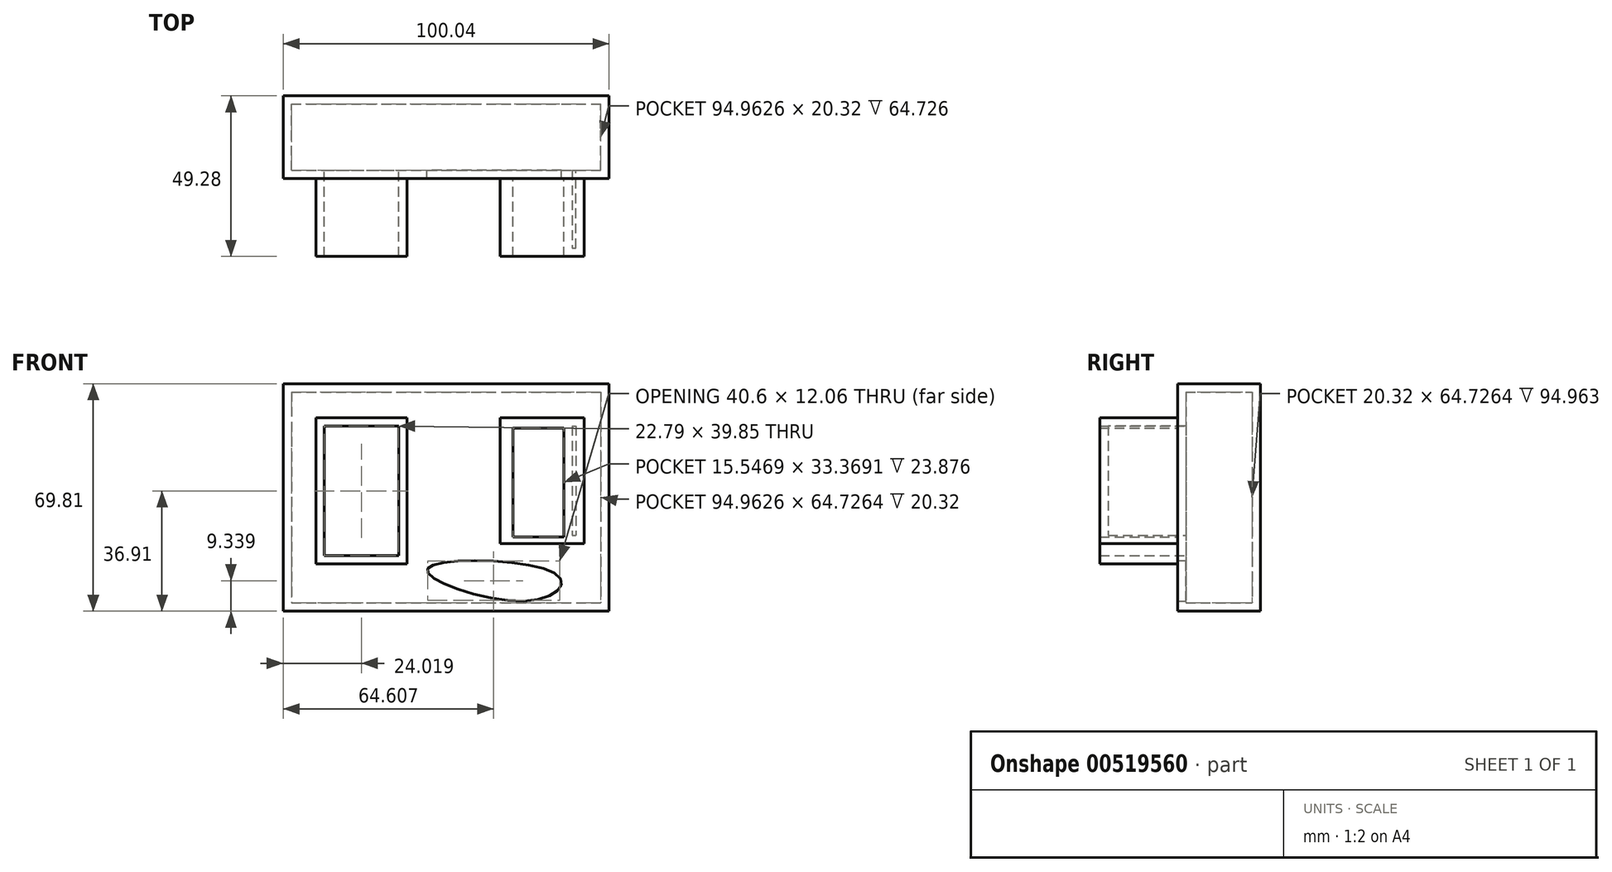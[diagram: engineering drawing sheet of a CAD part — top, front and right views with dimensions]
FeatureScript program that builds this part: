
annotation { "Feature Type Name" : "Feature", "Feature Type Description" : "" }
export const myFeature = defineFeature(function(context is Context, id is Id, definition is map)
    precondition{}
    {
        {
            var Q0;
            Q0=qCreatedBy(makeId("Front.planeOp"),FACE);
            var sketch = newSketch(context, id + "F0", { "sketchPlane" : qUnion([Q0])});
            skLineSegment(sketch, "E0.bottom", {"start": v(-54.26, 49.1) * mm, "end": v(45.78, 49.1) * mm});
            skLineSegment(sketch, "E0.top", {"start": v(-54.26, -20.7) * mm, "end": v(45.78, -20.7) * mm});
            skLineSegment(sketch, "E0.left", {"start": v(-54.26, 49.1) * mm, "end": v(-54.26, -20.7) * mm});
            skLineSegment(sketch, "E0.right", {"start": v(45.78, 49.1) * mm, "end": v(45.78, -20.7) * mm});
            skSolve(sketch);
        }
        {
            var Q0;
            Q0 = qSketchRegion(id + "F0", true);
            extrude(context, id + "F1", {"entities" : qUnion([Q0]), "depth" : 25.4 * mm, "offsetDistance" : 25.4 * mm});
        }
        {
            var Q0;
            Q0=makeQuery(id+"F1.opExtrude","CAP_FACE",FACE,{"disambiguationData":[OSD([sQuery(id+"F0.wireOp",EDGE,"E0.bottom"),sQuery(id+"F0.wireOp",EDGE,"E0.top"),sQuery(id+"F0.wireOp",EDGE,"E0.left"),sQuery(id+"F0.wireOp",EDGE,"E0.right")])],"isStart":false});
            var sketch = newSketch(context, id + "F2", { "sketchPlane" : qUnion([Q0])});
            skLineSegment(sketch, "E1.bottom", {"start": v(-44.18, 38.68) * mm, "end": v(-16.3, 38.68) * mm});
            skLineSegment(sketch, "E1.top", {"start": v(-44.18, 22) * mm, "end": v(-16.3, 22) * mm});
            skLineSegment(sketch, "E1.left", {"start": v(-44.18, 38.68) * mm, "end": v(-44.18, 22) * mm});
            skLineSegment(sketch, "E1.right", {"start": v(-16.3, 38.68) * mm, "end": v(-16.3, 22) * mm});
            skLineSegment(sketch, "E2.bottom", {"start": v(12.32, 38.68) * mm, "end": v(38.1, 38.68) * mm});
            skLineSegment(sketch, "E2.top", {"start": v(12.32, 0) * mm, "end": v(38.1, 0) * mm});
            skLineSegment(sketch, "E2.left", {"start": v(12.32, 38.68) * mm, "end": v(12.32, 0) * mm});
            skLineSegment(sketch, "E2.right", {"start": v(38.1, 38.68) * mm, "end": v(38.1, 0) * mm});
            skPoint(sketch, "E3.oppositeSnap0", {"position": v(-30.24, 22) * mm});
            skLineSegment(sketch, "E3.bottom", {"start": v(-30.24, 22) * mm, "end": v(-30.24, 22) * mm});
            skLineSegment(sketch, "E3.top", {"start": v(-30.24, 0) * mm, "end": v(-30.24, 0) * mm});
            skLineSegment(sketch, "E3.left", {"start": v(-30.24, 22) * mm, "end": v(-30.24, 0) * mm});
            skLineSegment(sketch, "E3.right", {"start": v(-30.24, 22) * mm, "end": v(-30.24, 0) * mm});
            skLineSegment(sketch, "E4.bottom", {"start": v(-16.3, 22) * mm, "end": v(-16.3, 22) * mm});
            skLineSegment(sketch, "E4.top", {"start": v(-16.3, 0) * mm, "end": v(-16.3, 0) * mm});
            skLineSegment(sketch, "E4.left", {"start": v(-16.3, 22) * mm, "end": v(-16.3, 0) * mm});
            skLineSegment(sketch, "E4.right", {"start": v(-16.3, 22) * mm, "end": v(-16.3, 0) * mm});
            skLineSegment(sketch, "E5.top", {"start": v(-44.18, -6.26) * mm, "end": v(-16.3, -6.26) * mm});
            skLineSegment(sketch, "E5.left", {"start": v(-44.18, 22) * mm, "end": v(-44.18, -6.26) * mm});
            skLineSegment(sketch, "E5.right", {"start": v(-16.3, 22) * mm, "end": v(-16.3, -6.26) * mm});
            skLineSegment(sketch, "E6.bottom", {"start": v(-16.3, -6.26) * mm, "end": v(-44.18, -6.26) * mm});
            skLineSegment(sketch, "E6.top", {"start": v(-16.3, 22) * mm, "end": v(-44.18, 22) * mm});
            skLineSegment(sketch, "E6.left", {"start": v(-16.3, -6.26) * mm, "end": v(-16.3, 22) * mm});
            skLineSegment(sketch, "E6.right", {"start": v(-44.18, -6.26) * mm, "end": v(-44.18, 22) * mm});
            skLineSegment(sketch, "E7.bottom", {"start": v(-44.18, 22) * mm, "end": v(-44.18, 22) * mm});
            skLineSegment(sketch, "E7.top", {"start": v(-44.18, 0) * mm, "end": v(-44.18, 0) * mm});
            skLineSegment(sketch, "E7.left", {"start": v(-44.18, 22) * mm, "end": v(-44.18, 0) * mm});
            skLineSegment(sketch, "E7.right", {"start": v(-44.18, 22) * mm, "end": v(-44.18, 0) * mm});
            skLineSegment(sketch, "E8.bottom", {"start": v(-16.3, -2.09) * mm, "end": v(-44.18, -2.09) * mm});
            skLineSegment(sketch, "E8.left", {"start": v(-16.3, -2.09) * mm, "end": v(-16.3, -6.26) * mm});
            skLineSegment(sketch, "E8.right", {"start": v(-44.18, -2.09) * mm, "end": v(-44.18, -6.26) * mm});
            skLineSegment(sketch, "E9.bottom", {"start": v(-44.18, -2.09) * mm, "end": v(-16.3, -2.09) * mm});
            skLineSegment(sketch, "E9.top", {"start": v(-44.18, -2.09) * mm, "end": v(-16.3, -2.09) * mm});
            skLineSegment(sketch, "E9.left", {"start": v(-44.18, -2.09) * mm, "end": v(-44.18, -2.09) * mm});
            skLineSegment(sketch, "E9.right", {"start": v(-16.3, -2.09) * mm, "end": v(-16.3, -2.09) * mm});
            skLineSegment(sketch, "E10.bottom", {"start": v(-16.3, 0) * mm, "end": v(-44.18, 0) * mm});
            skLineSegment(sketch, "E10.top", {"start": v(-16.3, 0) * mm, "end": v(-44.18, 0) * mm});
            skLineSegment(sketch, "E11.top", {"start": v(-44.18, 0) * mm, "end": v(-16.3, 0) * mm});
            skLineSegment(sketch, "E12.bottom", {"start": v(-22, 38.68) * mm, "end": v(-22.18, 38.68) * mm});
            skLineSegment(sketch, "E12.top", {"start": v(-22, 22) * mm, "end": v(-22.18, 22) * mm});
            skLineSegment(sketch, "E12.left", {"start": v(-22, 38.68) * mm, "end": v(-22, 22) * mm});
            skLineSegment(sketch, "E12.right", {"start": v(-22.18, 38.68) * mm, "end": v(-22.18, 22) * mm});
            skLineSegment(sketch, "E13.bottom", {"start": v(-37.92, 38.68) * mm, "end": v(-37.73, 38.68) * mm});
            skLineSegment(sketch, "E13.top", {"start": v(-37.92, 22) * mm, "end": v(-37.73, 22) * mm});
            skLineSegment(sketch, "E13.left", {"start": v(-37.92, 38.68) * mm, "end": v(-37.92, 22) * mm});
            skLineSegment(sketch, "E13.right", {"start": v(-37.73, 38.68) * mm, "end": v(-37.73, 22) * mm});
            skLineSegment(sketch, "E14.bottom", {"start": v(-44.18, 7.87) * mm, "end": v(-16.3, 7.87) * mm});
            skLineSegment(sketch, "E14.top", {"start": v(-44.18, 7.87) * mm, "end": v(-16.3, 7.87) * mm});
            skLineSegment(sketch, "E14.left", {"start": v(-44.18, 7.87) * mm, "end": v(-44.18, 7.87) * mm});
            skLineSegment(sketch, "E14.right", {"start": v(-16.3, 7.87) * mm, "end": v(-16.3, 7.87) * mm});
            skLineSegment(sketch, "E15.bottom", {"start": v(-16.3, 12.9) * mm, "end": v(-44.18, 12.9) * mm});
            skLineSegment(sketch, "E15.top", {"start": v(-16.3, 11) * mm, "end": v(-44.18, 11) * mm});
            skLineSegment(sketch, "E15.left", {"start": v(-16.3, 12.9) * mm, "end": v(-16.3, 11) * mm});
            skLineSegment(sketch, "E15.right", {"start": v(-44.18, 12.9) * mm, "end": v(-44.18, 11) * mm});
            skLineSegment(sketch, "E16.bottom", {"start": v(-44.18, 16.87) * mm, "end": v(-16.3, 16.87) * mm});
            skLineSegment(sketch, "E16.top", {"start": v(-44.18, 19.72) * mm, "end": v(-16.3, 19.72) * mm});
            skLineSegment(sketch, "E16.left", {"start": v(-44.18, 16.87) * mm, "end": v(-44.18, 19.72) * mm});
            skLineSegment(sketch, "E16.right", {"start": v(-16.3, 16.87) * mm, "end": v(-16.3, 19.72) * mm});
            skLineSegment(sketch, "E17.bottom", {"start": v(12.32, 6.45) * mm, "end": v(38.1, 6.45) * mm});
            skLineSegment(sketch, "E17.top", {"start": v(12.32, 7.77) * mm, "end": v(38.1, 7.77) * mm});
            skLineSegment(sketch, "E17.left", {"start": v(12.32, 6.45) * mm, "end": v(12.32, 7.77) * mm});
            skLineSegment(sketch, "E17.right", {"start": v(38.1, 6.45) * mm, "end": v(38.1, 7.77) * mm});
            skLineSegment(sketch, "E18.bottom", {"start": v(38.1, 11.38) * mm, "end": v(12.32, 11.38) * mm});
            skLineSegment(sketch, "E18.top", {"start": v(38.1, 12.9) * mm, "end": v(12.32, 12.9) * mm});
            skLineSegment(sketch, "E18.left", {"start": v(38.1, 11.38) * mm, "end": v(38.1, 12.9) * mm});
            skLineSegment(sketch, "E18.right", {"start": v(12.32, 11.38) * mm, "end": v(12.32, 12.9) * mm});
            skLineSegment(sketch, "E19.bottom", {"start": v(12.32, 17.44) * mm, "end": v(38.1, 17.44) * mm});
            skLineSegment(sketch, "E19.top", {"start": v(12.32, 15.36) * mm, "end": v(38.1, 15.36) * mm});
            skLineSegment(sketch, "E19.left", {"start": v(12.32, 17.44) * mm, "end": v(12.32, 15.36) * mm});
            skLineSegment(sketch, "E19.right", {"start": v(38.1, 17.44) * mm, "end": v(38.1, 15.36) * mm});
            skPoint(sketch, "E20.oppositeSnap0", {"position": v(12.32, 19.34) * mm});
            skLineSegment(sketch, "E20.bottom", {"start": v(38.1, 19.34) * mm, "end": v(12.32, 19.34) * mm});
            skLineSegment(sketch, "E20.top", {"start": v(38.1, 22) * mm, "end": v(12.32, 22) * mm});
            skLineSegment(sketch, "E20.left", {"start": v(38.1, 19.34) * mm, "end": v(38.1, 22) * mm});
            skLineSegment(sketch, "E20.right", {"start": v(12.32, 19.34) * mm, "end": v(12.32, 22) * mm});
            skLineSegment(sketch, "E21.bottom", {"start": v(12.32, 24.65) * mm, "end": v(38.1, 24.65) * mm});
            skLineSegment(sketch, "E21.top", {"start": v(12.32, 30.15) * mm, "end": v(38.1, 30.15) * mm});
            skLineSegment(sketch, "E21.left", {"start": v(12.32, 24.65) * mm, "end": v(12.32, 30.15) * mm});
            skLineSegment(sketch, "E21.right", {"start": v(38.1, 24.65) * mm, "end": v(38.1, 30.15) * mm});
            skLineSegment(sketch, "E22.bottom", {"start": v(16.3, 38.68) * mm, "end": v(21.42, 38.68) * mm});
            skLineSegment(sketch, "E22.top", {"start": v(16.3, 0) * mm, "end": v(21.42, 0) * mm});
            skLineSegment(sketch, "E22.left", {"start": v(16.3, 38.68) * mm, "end": v(16.3, 0) * mm});
            skLineSegment(sketch, "E22.right", {"start": v(21.42, 38.68) * mm, "end": v(21.42, 0) * mm});
            skLineSegment(sketch, "E23.bottom", {"start": v(26.73, 38.68) * mm, "end": v(31.85, 38.68) * mm});
            skLineSegment(sketch, "E23.top", {"start": v(26.73, 0) * mm, "end": v(31.85, 0) * mm});
            skLineSegment(sketch, "E23.left", {"start": v(26.73, 38.68) * mm, "end": v(26.73, 0) * mm});
            skLineSegment(sketch, "E23.right", {"start": v(31.85, 38.68) * mm, "end": v(31.85, 0) * mm});
            skLineSegment(sketch, "E24.bottom", {"start": v(12.32, 33.56) * mm, "end": v(38.1, 33.56) * mm});
            skLineSegment(sketch, "E24.top", {"start": v(12.32, 35.45) * mm, "end": v(38.1, 35.45) * mm});
            skLineSegment(sketch, "E24.left", {"start": v(12.32, 33.56) * mm, "end": v(12.32, 35.45) * mm});
            skLineSegment(sketch, "E24.right", {"start": v(38.1, 33.56) * mm, "end": v(38.1, 35.45) * mm});
            skLineSegment(sketch, "E25.bottom", {"start": v(12.32, 3.6) * mm, "end": v(38.1, 3.6) * mm});
            skLineSegment(sketch, "E25.top", {"start": v(12.32, 2.09) * mm, "end": v(38.1, 2.09) * mm});
            skLineSegment(sketch, "E25.left", {"start": v(12.32, 3.6) * mm, "end": v(12.32, 2.09) * mm});
            skLineSegment(sketch, "E25.right", {"start": v(38.1, 3.6) * mm, "end": v(38.1, 2.09) * mm});
            skSolve(sketch);
        }
        {
            var Q0;
            Q0 = qSketchRegion(id + "F2", true);
            extrude(context, id + "F3", {"entities" : qUnion([Q0]), "operationType" : NewBodyOperationType.ADD, "depth" : 23.88 * mm, "offsetDistance" : 25.4 * mm});
        }
        {
            var Q0;
            Q0=makeQuery(id+"F3.opExtrude","CAP_FACE",FACE,{"disambiguationData":[OSD([sQuery(id+"F2.wireOp",EDGE,"E1.bottom"),sQuery(id+"F2.wireOp",EDGE,"E1.left"),sQuery(id+"F2.wireOp",EDGE,"E1.right"),sQuery(id+"F2.wireOp",EDGE,"E6.left"),sQuery(id+"F2.wireOp",EDGE,"E6.right"),sQuery(id+"F2.wireOp",EDGE,"E6.bottom"),sQuery(id+"F2.wireOp",EDGE,"E8.left"),sQuery(id+"F2.wireOp",EDGE,"E8.right"),sQuery(id+"F2.wireOp",EDGE,"E7.left"),sQuery(id+"F2.wireOp",EDGE,"E4.left"),sQuery(id+"F2.wireOp",EDGE,"E12.bottom"),sQuery(id+"F2.wireOp",EDGE,"E13.bottom"),sQuery(id+"F2.wireOp",EDGE,"E15.left"),sQuery(id+"F2.wireOp",EDGE,"E15.right"),sQuery(id+"F2.wireOp",EDGE,"E16.left"),sQuery(id+"F2.wireOp",EDGE,"E16.right")])],"isStart":false});
            shell(context, id + "F4", {"entities" : qUnion([Q0]), "thickness" : 2.54 * mm});
        }
        {
            var Q0;
            {var subQ0=sQuery(id+"F0.wireOp",EDGE,"E0.bottom");var subQ1=sQuery(id+"F0.wireOp",EDGE,"E0.right");var subQ2=sQuery(id+"F0.wireOp",EDGE,"E0.top");var subQ3=sQuery(id+"F0.wireOp",EDGE,"E0.left");Q0=makeQuery(id+"F3.boolean.opBoolean","SPLIT",FACE,{"disambiguationData":[TD([makeQuery(id+"F1.opExtrude","SWEPT_FACE",FACE,{"disambiguationData":[OSD([subQ0])]})])],"derivedFrom":makeQuery(id+"F1.opExtrude","CAP_FACE",FACE,{"disambiguationData":[OSD([subQ0,subQ2,subQ3,subQ1])],"isStart":false})});}
            var sketch = newSketch(context, id + "F5", { "sketchPlane" : qUnion([Q0])});
            skFitSpline(sketch, "E26", {"points": [v(-9.96, -7.64) * mm, v(30.04, -9.77) * mm, v(22.8, -17.34) * mm, v(-9.96, -7.64) * mm]});
            skSolve(sketch);
        }
        {
            var Q0;
            Q0 = qSketchRegion(id + "F5", true);
            extrude(context, id + "F6", {"entities" : qUnion([Q0]), "operationType" : NewBodyOperationType.REMOVE, "oppositeDirection" : true, "depth" : 8.9 * mm, "offsetDistance" : 25.4 * mm});
        }
    });
